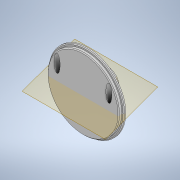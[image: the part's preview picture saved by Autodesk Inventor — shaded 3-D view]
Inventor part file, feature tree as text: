
AUTODESK INVENTOR PART (.ipt)
format: ipt  version: 2021 (Build 250183000, 183)  size: 172,544 bytes
history: native  units: in
note: dims shown in document units (in); Inventor stores cm internally (conversion verified against a paired STEP export)
features: extrude x4, sketch x4, chamfer x2, fillet x1, plane x1, mirror x1, projected_geometry x1
ambient origin geometry x8: Origin, YZ Plane, XZ Plane, XY Plane, X Axis, Y Axis, Z Axis, Center Point
bodies: Solid1 (feature_tree)
feature tree (14):
  extrude  "Extrusion1"  Depth=0.0394in TaperAngle=0.0deg
  extrude  "Extrusion2"  Depth=0.0591in TaperAngle=0.0deg
  chamfer  "Chamfer1"  Distance=0.0787in Angle=45.0deg
  chamfer  "Chamfer2"  Distance=0.0787in Angle=45.0deg
  extrude  "Extrusion3"  Depth=0.3937in
  fillet  "Fillet1"  Radius=0.1969in
  plane  "Work Plane1"
  extrude  "Extrusion4"  Depth=0.5118in
  mirror  "Mirror1"
  sketch  "Sketch1"  dims[d0=1.4961in d1=0.0394in d2=0.0in]
  sketch  "Sketch2"  dims[d3=1.4134in d4=0.0591in d5=0.0in d6=0.0157in d7=0.0787in d8=45.0deg d9=0.0157in d10=0.0787in d11=45.0deg]
  sketch  "Sketch3"  dims[d12=0.1575in d13=0.3937in d14=0.1374in d15=0.1969in]
  sketch  "Sketch4"  dims[d16=0.1374in d17=0.1181in d18=0.5118in d19=0.0in d20=0.0in d21=0.0197in d22=0.0344in d23=0.0197in d24=0.0344in]
  projected_geometry  "Projected Loop1"
